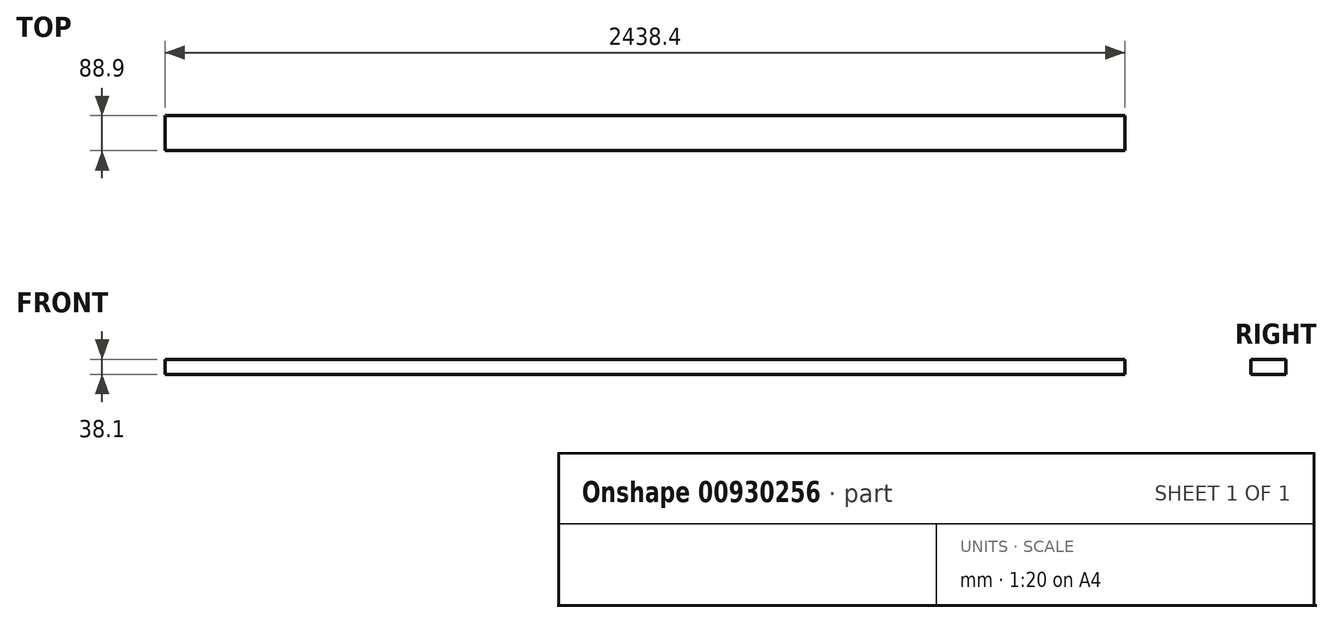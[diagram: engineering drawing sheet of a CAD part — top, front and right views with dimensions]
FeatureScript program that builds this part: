
annotation { "Feature Type Name" : "Feature", "Feature Type Description" : "" }
export const myFeature = defineFeature(function(context is Context, id is Id, definition is map)
    precondition{}
    {
        {
            var Q0;
            Q0=qCreatedBy(makeId("Right.planeOp"),FACE);
            var sketch = newSketch(context, id + "F0", { "sketchPlane" : qUnion([Q0])});
            skLineSegment(sketch, "E0.bottom", {"start": v(44.45, -19.05) * mm, "end": v(-44.45, -19.05) * mm});
            skLineSegment(sketch, "E0.top", {"start": v(44.45, 19.05) * mm, "end": v(-44.45, 19.05) * mm});
            skLineSegment(sketch, "E0.left", {"start": v(44.45, -19.05) * mm, "end": v(44.45, 19.05) * mm});
            skLineSegment(sketch, "E0.right", {"start": v(-44.45, -19.05) * mm, "end": v(-44.45, 19.05) * mm});
            skPoint(sketch, "E0.middle", {"position": v(0, 0) * mm});
            skSolve(sketch);
        }
        {
            var Q0;
            Q0=qSketchRegion(id+"F0",true);
            extrude(context, id + "F1", {"entities" : qUnion([Q0]), "endBound" : BoundingType.SYMMETRIC, "depth" : 2438.4 * mm});
        }
    });
